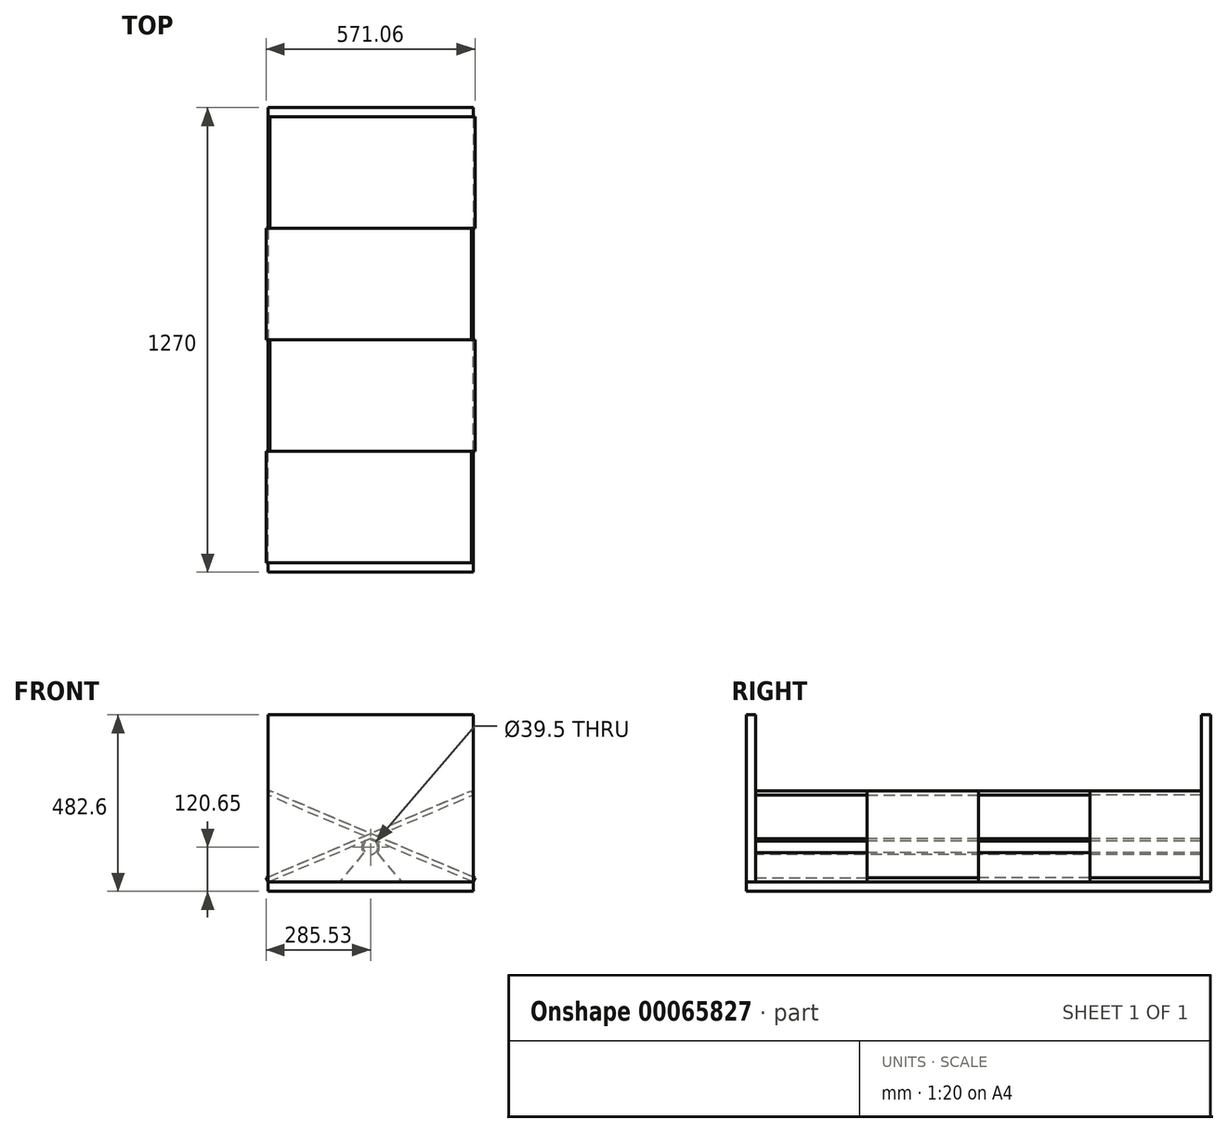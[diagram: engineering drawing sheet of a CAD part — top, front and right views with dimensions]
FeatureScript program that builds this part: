
annotation { "Feature Type Name" : "Feature", "Feature Type Description" : "" }
export const myFeature = defineFeature(function(context is Context, id is Id, definition is map)
    precondition{}
    {
        {
            var Q0;
            Q0=qCreatedBy(makeId("Top.planeOp"),FACE);
            var sketch = newSketch(context, id + "F0", { "sketchPlane" : qUnion([Q0])});
            skLineSegment(sketch, "E0.rect.bottom", {"start": v(-280.57, 609.6) * mm, "end": v(280.57, 609.6) * mm});
            skLineSegment(sketch, "E0.rect.top", {"start": v(-280.57, -609.6) * mm, "end": v(280.57, -609.6) * mm});
            skLineSegment(sketch, "E0.rect.left", {"start": v(-280.57, 609.6) * mm, "end": v(-280.57, -609.6) * mm});
            skLineSegment(sketch, "E0.rect.right", {"start": v(280.57, 609.6) * mm, "end": v(280.57, -609.6) * mm});
            skPoint(sketch, "E0.rect.middle", {"position": v(0, 0) * mm});
            skLineSegment(sketch, "E1.rect.bottom", {"start": v(-280.57, 635) * mm, "end": v(280.57, 635) * mm});
            skLineSegment(sketch, "E1.rect.top", {"start": v(-280.57, -635) * mm, "end": v(280.57, -635) * mm});
            skLineSegment(sketch, "E1.rect.left", {"start": v(-280.57, 635) * mm, "end": v(-280.57, -635) * mm});
            skLineSegment(sketch, "E1.rect.right", {"start": v(280.57, 635) * mm, "end": v(280.57, -635) * mm});
            skSolve(sketch);
        }
        {
            var Q0;
            Q0=qCreatedBy(makeId("Front.planeOp"),FACE);
            var sketch = newSketch(context, id + "F1", { "sketchPlane" : qUnion([Q0])});
            skLineSegment(sketch, "E2", {"start": v(0, 119.1) * mm, "end": v(-280.57, 0) * mm});
            skLineSegment(sketch, "E3", {"start": v(0, 119.1) * mm, "end": v(280.57, 238.19) * mm});
            skLineSegment(sketch, "E4", {"start": v(-280.57, 0) * mm, "end": v(-285.53, 11.7) * mm});
            skLineSegment(sketch, "E5", {"start": v(-285.53, 11.7) * mm, "end": v(275.6, 249.88) * mm});
            skLineSegment(sketch, "E6", {"start": v(280.57, 238.19) * mm, "end": v(275.6, 249.88) * mm});
            skLineSegment(sketch, "E7.MirrorCS", {"start": v(-280.57, 238.19) * mm, "end": v(-275.6, 249.88) * mm});
            skLineSegment(sketch, "E8.MirrorCS", {"start": v(280.57, 0) * mm, "end": v(285.53, 11.7) * mm});
            skLineSegment(sketch, "E9.MirrorCS", {"start": v(0, 119.1) * mm, "end": v(280.57, 0) * mm});
            skLineSegment(sketch, "E10.MirrorCS", {"start": v(285.53, 11.7) * mm, "end": v(-275.6, 249.88) * mm});
            skLineSegment(sketch, "E11.MirrorCS", {"start": v(0, 119.1) * mm, "end": v(-280.57, 238.19) * mm});
            skCircle(sketch, "E12", {"center": v(0, 95.25) * mm, "radius": 23.84 * mm});
            skLineSegment(sketch, "E13", {"start": v(-18.26, 79.92) * mm, "end": v(-84.98, 0) * mm});
            skLineSegment(sketch, "E14.MirrorCS", {"start": v(18.26, 79.92) * mm, "end": v(84.98, 0) * mm});
            skLineSegment(sketch, "E15", {"start": v(84.98, 0) * mm, "end": v(-84.98, 0) * mm});
            skCircle(sketch, "E16", {"center": v(0, 95.25) * mm, "radius": 19.75 * mm});
            skSolve(sketch);
        }
        {
            var Q0;
            {var subQ5=sQuery(id+"F1.wireOp",EDGE,"E7.MirrorCS");Q0=makeQuery(id+"F1.imprint","IMPRINT",FACE,{"disambiguationData":[TD([[makeQuery(id+"F1.imprint","IMPRINT",EDGE,{"derivedFrom":subQ5}),-1.0]])]});}
            var Q1;
            {var subQ1=sQuery(id+"F1.wireOp",EDGE,"E8.MirrorCS");Q1=makeQuery(id+"F1.imprint","IMPRINT",FACE,{"disambiguationData":[TD([[makeQuery(id+"F1.imprint","IMPRINT",EDGE,{"derivedFrom":subQ1}),1.0]])]});}
            var Q2;
            {var subQ0=sQuery(id+"F1.wireOp",EDGE,"E11.MirrorCS");var subQ5=sQuery(id+"F1.wireOp",EDGE,"E5");var subQ6=makeQuery(id+"F1.imprint","INTERSECT",VERTEX,{"derivedFrom":[subQ5,subQ0]});Q2=makeQuery(id+"F1.imprint","IMPRINT",FACE,{"disambiguationData":[TD([[makeQuery(id+"F1.imprint","IMPRINT",EDGE,{"disambiguationData":[TD([[subQ6,-1.0]])],"derivedFrom":subQ5}),-1.0]])]});}
            var Q3;
            {var subQ0=sQuery(id+"F1.wireOp",EDGE,"E12");var subQ1=sQuery(id+"F1.wireOp",EDGE,"E9.MirrorCS");var subQ3=makeQuery(id+"F1.imprint","INTERSECT",VERTEX,{"derivedFrom":[subQ1,subQ0]});Q3=makeQuery(id+"F1.imprint","IMPRINT",FACE,{"disambiguationData":[TD([[makeQuery(id+"F1.imprint","IMPRINT",EDGE,{"disambiguationData":[TD([[subQ3,1.0]])],"derivedFrom":subQ1}),1.0]])]});}
            extrude(context, id + "F2", {"entities" : qUnion([Q0, Q1, Q2, Q3]), "depth" : 304.8 * mm});
        }
        {
            var Q0;
            Q0=makeQuery(id+"F2.opExtrude","CAP_FACE",FACE,{"disambiguationData":[OSD([sQuery(id+"F1.wireOp",EDGE,"E7.MirrorCS"),sQuery(id+"F1.wireOp",EDGE,"E8.MirrorCS"),sQuery(id+"F1.wireOp",EDGE,"E9.MirrorCS"),sQuery(id+"F1.wireOp",EDGE,"E10.MirrorCS"),sQuery(id+"F1.wireOp",EDGE,"E11.MirrorCS")])],"isStart":false});
            extrude(context, id + "F3", {"entities" : qUnion([Q0]), "operationType" : NewBodyOperationType.ADD, "oppositeDirection" : true, "depth" : 914.4 * mm, "hasSecondDirection" : true, "secondDirectionOppositeDirection" : true, "secondDirectionDepth" : 609.6 * mm});
        }
        {
            var Q0;
            {var subQ0=sQuery(id+"F1.wireOp",EDGE,"E6");Q0=makeQuery(id+"F1.imprint","IMPRINT",FACE,{"disambiguationData":[TD([[makeQuery(id+"F1.imprint","IMPRINT",EDGE,{"derivedFrom":subQ0}),1.0]])]});}
            var Q1;
            {var subQ0=sQuery(id+"F1.wireOp",EDGE,"E11.MirrorCS");var subQ5=sQuery(id+"F1.wireOp",EDGE,"E5");var subQ6=makeQuery(id+"F1.imprint","INTERSECT",VERTEX,{"derivedFrom":[subQ5,subQ0]});Q1=makeQuery(id+"F1.imprint","IMPRINT",FACE,{"disambiguationData":[TD([[makeQuery(id+"F1.imprint","IMPRINT",EDGE,{"disambiguationData":[TD([[subQ6,-1.0]])],"derivedFrom":subQ5}),-1.0]])]});}
            var Q2;
            {var subQ0=sQuery(id+"F1.wireOp",EDGE,"E12");var subQ1=sQuery(id+"F1.wireOp",EDGE,"E2");var subQ3=makeQuery(id+"F1.imprint","INTERSECT",VERTEX,{"derivedFrom":[subQ1,subQ0]});Q2=makeQuery(id+"F1.imprint","IMPRINT",FACE,{"disambiguationData":[TD([[makeQuery(id+"F1.imprint","IMPRINT",EDGE,{"disambiguationData":[TD([[subQ3,1.0]])],"derivedFrom":subQ1}),-1.0]])]});}
            var Q3;
            {var subQ6=sQuery(id+"F1.wireOp",EDGE,"E4");Q3=makeQuery(id+"F1.imprint","IMPRINT",FACE,{"disambiguationData":[TD([[makeQuery(id+"F1.imprint","IMPRINT",EDGE,{"derivedFrom":subQ6}),-1.0]])]});}
            extrude(context, id + "F4", {"entities" : qUnion([Q0, Q1, Q2, Q3]), "oppositeDirection" : true, "depth" : 304.8 * mm});
        }
        {
            var Q0;
            Q0=makeQuery(id+"F4.opExtrude","CAP_FACE",FACE,{"disambiguationData":[OSD([sQuery(id+"F1.wireOp",EDGE,"E2"),sQuery(id+"F1.wireOp",EDGE,"E3"),sQuery(id+"F1.wireOp",EDGE,"E4"),sQuery(id+"F1.wireOp",EDGE,"E5"),sQuery(id+"F1.wireOp",EDGE,"E6")])],"isStart":true});
            extrude(context, id + "F5", {"entities" : qUnion([Q0]), "depth" : 609.6 * mm, "hasSecondDirection" : true, "secondDirectionOppositeDirection" : false, "secondDirectionDepth" : 304.8 * mm});
        }
        {
            var Q0;
            Q0=makeQuery(id+"F1.imprint","IMPRINT",FACE,{"disambiguationData":[TD([[makeQuery(id+"F1.imprint","IMPRINT",EDGE,{"derivedFrom":sQuery(id+"F1.wireOp",EDGE,"E16")}),-1.0]])]});
            var Q1;
            {var subQ0=sQuery(id+"F1.wireOp",EDGE,"E13");Q1=makeQuery(id+"F1.imprint","IMPRINT",FACE,{"disambiguationData":[TD([[makeQuery(id+"F1.imprint","IMPRINT",EDGE,{"derivedFrom":subQ0}),1.0]])]});}
            extrude(context, id + "F6", {"entities" : qUnion([Q0, Q1]), "oppositeDirection" : true, "depth" : 609.6 * mm, "hasSecondDirection" : true, "secondDirectionOppositeDirection" : false, "secondDirectionDepth" : 609.6 * mm});
        }
        {
            var Q0;
            {var subQ0=sQuery(id+"F0.wireOp",EDGE,"E0.rect.bottom");Q0=makeQuery(id+"F0.imprint","IMPRINT",FACE,{"disambiguationData":[TD([[makeQuery(id+"F0.imprint","IMPRINT",EDGE,{"derivedFrom":subQ0}),1.0]])]});}
            var Q1;
            {var subQ0=sQuery(id+"F0.wireOp",EDGE,"E0.rect.top");Q1=makeQuery(id+"F0.imprint","IMPRINT",FACE,{"disambiguationData":[TD([[makeQuery(id+"F0.imprint","IMPRINT",EDGE,{"derivedFrom":subQ0}),-1.0]])]});}
            extrude(context, id + "F7", {"entities" : qUnion([Q0, Q1]), "depth" : 457.2 * mm});
        }
        {
            var Q0;
            {var subQ0=sQuery(id+"F0.wireOp",EDGE,"E0.rect.bottom");Q0=makeQuery(id+"F0.imprint","IMPRINT",FACE,{"disambiguationData":[TD([[makeQuery(id+"F0.imprint","IMPRINT",EDGE,{"derivedFrom":subQ0}),-1.0]])]});}
            var Q1;
            {var subQ0=sQuery(id+"F0.wireOp",EDGE,"E0.rect.top");Q1=makeQuery(id+"F0.imprint","IMPRINT",FACE,{"disambiguationData":[TD([[makeQuery(id+"F0.imprint","IMPRINT",EDGE,{"derivedFrom":subQ0}),-1.0]])]});}
            var Q2;
            {var subQ0=sQuery(id+"F0.wireOp",EDGE,"E0.rect.bottom");Q2=makeQuery(id+"F0.imprint","IMPRINT",FACE,{"disambiguationData":[TD([[makeQuery(id+"F0.imprint","IMPRINT",EDGE,{"derivedFrom":subQ0}),1.0]])]});}
            extrude(context, id + "F8", {"entities" : qUnion([Q0, Q1, Q2]), "oppositeDirection" : true, "depth" : 25.4 * mm});
        }
    });
